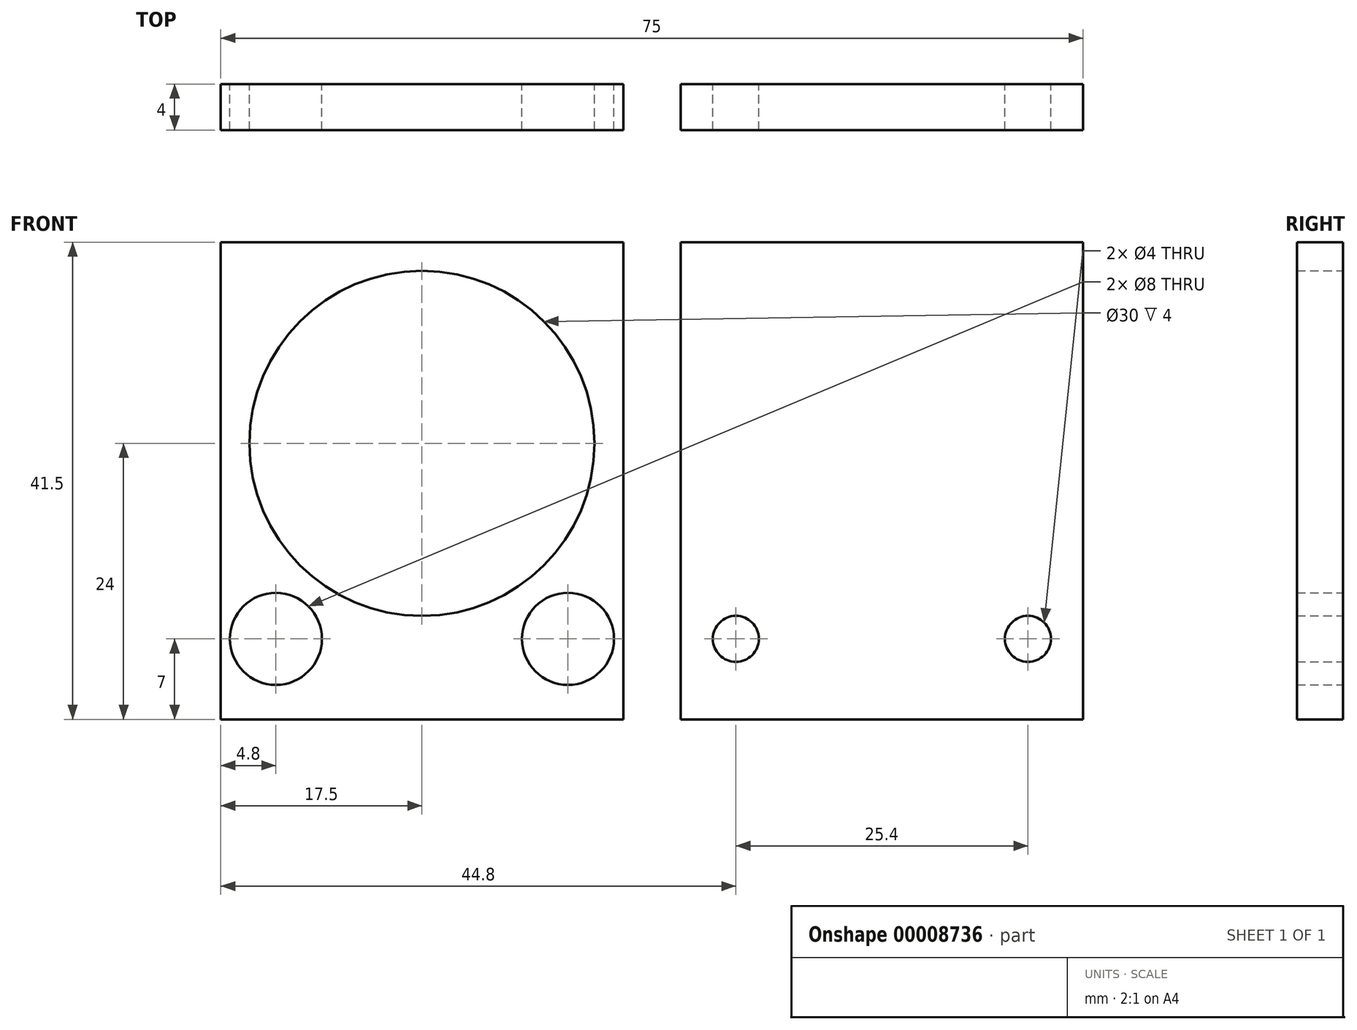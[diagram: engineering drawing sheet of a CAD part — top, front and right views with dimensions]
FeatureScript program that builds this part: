
annotation { "Feature Type Name" : "Feature", "Feature Type Description" : "" }
export const myFeature = defineFeature(function(context is Context, id is Id, definition is map)
    precondition{}
    {
        {
            var Q0;
            Q0=qCreatedBy(makeId("Front.planeOp"),FACE);
            var sketch = newSketch(context, id + "F0", { "sketchPlane" : qUnion([Q0])});
            skCircle(sketch, "E0", {"center": v(-12.7, 0) * mm, "radius": 4 * mm});
            skCircle(sketch, "E1", {"center": v(12.7, 0) * mm, "radius": 4 * mm});
            skLineSegment(sketch, "E2", {"start": v(-12.7, 0) * mm, "end": v(12.7, 0) * mm, "construction": true});
            skLineSegment(sketch, "E3.bottom", {"start": v(-17.5, 2) * mm, "end": v(17.5, 2) * mm, "construction": true});
            skLineSegment(sketch, "E3.top", {"start": v(-17.5, -7) * mm, "end": v(17.5, -7) * mm});
            skLineSegment(sketch, "E3.left", {"start": v(-17.5, 2) * mm, "end": v(-17.5, -7) * mm});
            skLineSegment(sketch, "E3.right", {"start": v(17.5, 2) * mm, "end": v(17.5, -7) * mm});
            skLineSegment(sketch, "E4", {"start": v(0, 2) * mm, "end": v(0, 0) * mm, "construction": true});
            skCircle(sketch, "E5", {"center": v(0, 17) * mm, "radius": 15 * mm});
            skLineSegment(sketch, "E6", {"start": v(-17.5, 2) * mm, "end": v(-17.5, 34.5) * mm});
            skLineSegment(sketch, "E7", {"start": v(-17.5, 34.5) * mm, "end": v(17.5, 34.5) * mm});
            skLineSegment(sketch, "E8", {"start": v(17.5, 34.5) * mm, "end": v(17.5, 2) * mm});
            skCircle(sketch, "E9", {"center": v(-12.7, 0) * mm, "radius": 7.5 * mm, "construction": true});
            skSolve(sketch);
        }
        {
            var Q0;
            Q0 = qSketchRegion(id + "F0", true);
            extrude(context, id + "F1", {"entities" : qUnion([Q0]), "depth" : 4 * mm});
        }
        {
            var Q0;
            Q0=qCreatedBy(makeId("Front.planeOp"),FACE);
            var sketch = newSketch(context, id + "F2", { "sketchPlane" : qUnion([Q0])});
            skLineSegment(sketch, "E10.bottom", {"start": v(22.5, -7) * mm, "end": v(57.5, -7) * mm});
            skLineSegment(sketch, "E10.top", {"start": v(22.5, 34.5) * mm, "end": v(57.5, 34.5) * mm});
            skLineSegment(sketch, "E10.left", {"start": v(22.5, -7) * mm, "end": v(22.5, 34.5) * mm});
            skLineSegment(sketch, "E10.right", {"start": v(57.5, -7) * mm, "end": v(57.5, 34.5) * mm});
            skCircle(sketch, "E11", {"center": v(27.3, 0) * mm, "radius": 2 * mm});
            skCircle(sketch, "E12", {"center": v(52.7, 0) * mm, "radius": 2 * mm});
            skLineSegment(sketch, "E13", {"start": v(40, -7) * mm, "end": v(40, 34.5) * mm, "construction": true});
            skLineSegment(sketch, "E14", {"start": v(27.3, 0) * mm, "end": v(40, 0) * mm, "construction": true});
            skLineSegment(sketch, "E15", {"start": v(40, 0) * mm, "end": v(52.7, 0) * mm, "construction": true});
            skLineSegment(sketch, "E16", {"start": v(58.5, 46.03) * mm, "end": v(58.5, -15) * mm, "construction": true});
            skLineSegment(sketch, "E17", {"start": v(22.5, 34.5) * mm, "end": v(22.5, 40.5) * mm, "construction": true});
            skLineSegment(sketch, "E18", {"start": v(22.5, 40.5) * mm, "end": v(22.5, 82) * mm, "construction": true});
            skLineSegment(sketch, "E19", {"start": v(22.5, 82) * mm, "end": v(57.5, 82) * mm, "construction": true});
            skLineSegment(sketch, "E20", {"start": v(57.5, 82) * mm, "end": v(57.5, 40.5) * mm, "construction": true});
            skLineSegment(sketch, "E21", {"start": v(57.5, 40.5) * mm, "end": v(57.5, 34.5) * mm, "construction": true});
            skLineSegment(sketch, "E22", {"start": v(22.5, 37.5) * mm, "end": v(57.5, 37.5) * mm, "construction": true});
            skCircle(sketch, "E23.0.MirrorC", {"center": v(27.3, 75) * mm, "radius": 2 * mm, "construction": true});
            skCircle(sketch, "E24.0.MirrorC", {"center": v(52.7, 75) * mm, "radius": 2 * mm, "construction": true});
            skSolve(sketch);
        }
        {
            var Q0;
            Q0 = qSketchRegion(id + "F2", true);
            extrude(context, id + "F3", {"entities" : qUnion([Q0]), "depth" : 4 * mm});
        }
    });
